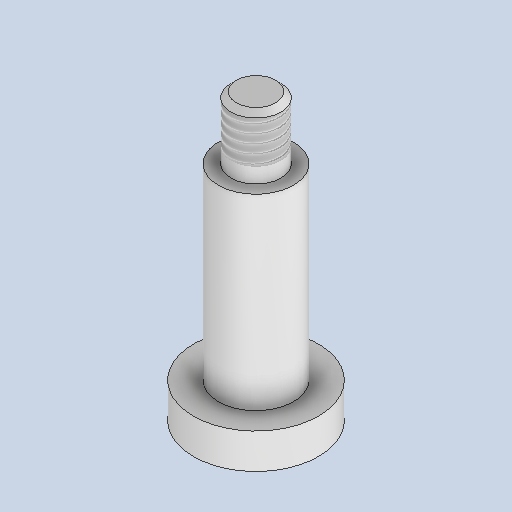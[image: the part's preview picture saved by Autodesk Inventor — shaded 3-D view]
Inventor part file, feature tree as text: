
AUTODESK INVENTOR PART (.ipt)
format: ipt  version: 2024.2 (Build 282272000, 272)  size: 141,312 bytes
history: native  units: mm
features: sketch x2, revolve x1, thread x1, extrude x1, chamfer x1
ambient origin geometry x8: Origin, YZ Plane, XZ Plane, XY Plane, X Axis, Y Axis, Z Axis, Center Point
bodies: Solid1 (feature_tree)
feature tree (6):
  revolve  "Revolution1"  [1 undecoded]
  thread  "Thread1"  [1 undecoded]
  extrude  "Extrusion1"  Depth=15.0mm
  chamfer  "Chamfer1"  Distance=2.8mm
  sketch  "Sketch1"  dims[d0=10.0mm d1=6.0mm d2=4.0mm]
  sketch  "Sketch2"  dims[d3=5.0mm d4=15.0mm d5=2.8mm d6=90.0deg d7=6.0mm d8=1.2mm d9=2.5mm d10=2.0mm d11=0.0mm d12=0.43mm d13=2.0mm d14=45.0deg]
note: 2 required parameter values undecoded (feature->parameter linkage not recoverable at this tier; creation-order binding heuristic only, values carry confidence <= 0.55)